# Revit family: Einbaugeräte_Modul_45-Systeme_Steckdose_0°_Schutzkontakt_3_fach
name_source: partatom
category: Generic Models
revit_build: Autodesk Revit 2015 (Build: 20140606_1530(x64)
units: mm (PartAtom-declared; Revit-internal decimal feet)

## types (6) — shared parameters
Manufacturer = OBO Bettermann
URL = http://www.obo-bettermann.com

## per-type parameters (varying)
| type | GTIN | Manufacturer Art. No. | Material |
| STD-D0 MZGN3 | 4012196047321 | 6120046 | Polycarbonate, minzgrün |
| STD-D0 ROR3 | 4012196047277 | 6120044 | Polycarbonate, reinorange |
| STD-D0 RW3 | 4012196047260 | 6120042 | Polycarbonate, Clear reinweiß |
| STD-D0 SRO3 | 4012196047345 | 6120048 | Polycarbonate, signalrot |
| STD-D0 AL3 | 4012196047390 | 6120052 | Polycarbonate,Alu lackiert |
| STD-D0 SWGR3 | 4012196047383 | 6120050 | Polycarbonate, schwarzgrau |

note: column(s) folded — value = type name in every type: Article Type

## geometry (parser evidence)
native form markers: Sweep x2
no freeform markers — native parametric forms only
